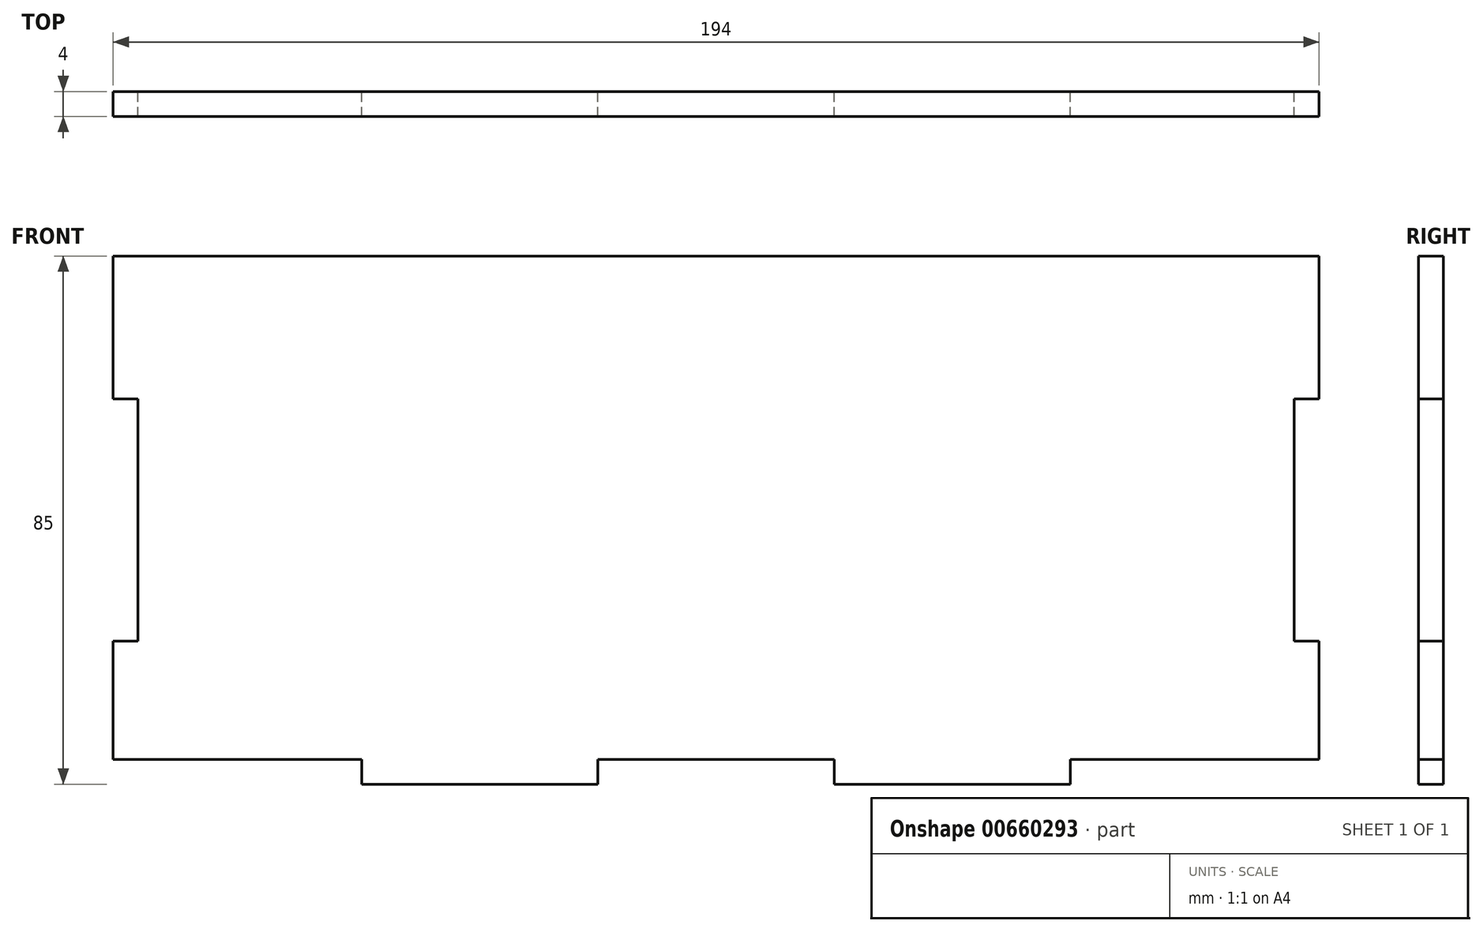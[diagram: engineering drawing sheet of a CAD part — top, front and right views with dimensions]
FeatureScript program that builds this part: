
annotation { "Feature Type Name" : "Feature", "Feature Type Description" : "" }
export const myFeature = defineFeature(function(context is Context, id is Id, definition is map)
    precondition{}
    {
        {
            var Q0;
            Q0=qCreatedBy(makeId("Front.planeOp"),FACE);
            var sketch = newSketch(context, id + "F0", { "sketchPlane" : qUnion([Q0])});
            skLineSegment(sketch, "E0.bottom", {"start": v(0, 0) * mm, "end": v(194, 0) * mm});
            skLineSegment(sketch, "E0.top", {"start": v(0, 85) * mm, "end": v(194, 85) * mm});
            skLineSegment(sketch, "E0.left", {"start": v(0, 0) * mm, "end": v(0, 85) * mm});
            skLineSegment(sketch, "E0.right", {"start": v(194, 0) * mm, "end": v(194, 85) * mm});
            skLineSegment(sketch, "E1.bottom", {"start": v(0, 0) * mm, "end": v(40, 0) * mm});
            skLineSegment(sketch, "E1.top", {"start": v(0, 4) * mm, "end": v(40, 4) * mm});
            skLineSegment(sketch, "E1.left", {"start": v(0, 0) * mm, "end": v(0, 4) * mm});
            skLineSegment(sketch, "E1.right", {"start": v(40, 0) * mm, "end": v(40, 4) * mm});
            skLineSegment(sketch, "E2.bottom", {"start": v(78, 0) * mm, "end": v(116, 0) * mm});
            skLineSegment(sketch, "E2.top", {"start": v(78, 4) * mm, "end": v(116, 4) * mm});
            skLineSegment(sketch, "E2.left", {"start": v(78, 0) * mm, "end": v(78, 4) * mm});
            skLineSegment(sketch, "E2.right", {"start": v(116, 0) * mm, "end": v(116, 4) * mm});
            skLineSegment(sketch, "E3.bottom", {"start": v(194, 0) * mm, "end": v(154, 0) * mm});
            skLineSegment(sketch, "E3.top", {"start": v(194, 4) * mm, "end": v(154, 4) * mm});
            skLineSegment(sketch, "E3.left", {"start": v(194, 0) * mm, "end": v(194, 4) * mm});
            skLineSegment(sketch, "E3.right", {"start": v(154, 0) * mm, "end": v(154, 4) * mm});
            skLineSegment(sketch, "E4.bottom", {"start": v(0, 62) * mm, "end": v(4, 62) * mm});
            skLineSegment(sketch, "E4.top", {"start": v(0, 23) * mm, "end": v(4, 23) * mm});
            skLineSegment(sketch, "E4.left", {"start": v(0, 62) * mm, "end": v(0, 23) * mm});
            skLineSegment(sketch, "E4.right", {"start": v(4, 62) * mm, "end": v(4, 23) * mm});
            skLineSegment(sketch, "E5.bottom", {"start": v(194, 62) * mm, "end": v(190, 62) * mm});
            skLineSegment(sketch, "E5.top", {"start": v(194, 23) * mm, "end": v(190, 23) * mm});
            skLineSegment(sketch, "E5.left", {"start": v(194, 62) * mm, "end": v(194, 23) * mm});
            skLineSegment(sketch, "E5.right", {"start": v(190, 62) * mm, "end": v(190, 23) * mm});
            skSolve(sketch);
        }
        {
            var Q0;
            {var subQ4=sQuery(id+"F0.wireOp",EDGE,"E0.top");Q0=makeQuery(id+"F0.imprint","IMPRINT",FACE,{"disambiguationData":[TD([[makeQuery(id+"F0.imprint","IMPRINT",EDGE,{"derivedFrom":subQ4}),-1.0]])]});}
            extrude(context, id + "F1", {"entities" : qUnion([Q0]), "depth" : 4 * mm, "offsetDistance" : 25 * mm});
        }
    });
